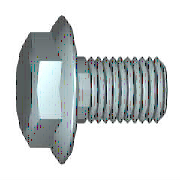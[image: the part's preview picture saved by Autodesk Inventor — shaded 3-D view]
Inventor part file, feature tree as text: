
AUTODESK INVENTOR PART (.ipt)
format: ipt  version: 2018 (Build 220112000, 112)  size: 210,944 bytes
history: native  units: mm (DEFAULTED — no unit token found)
features: sketch x3, other x2, extrude x1, plane x1
ambient origin geometry x7: Origin, YZ Plane, XZ Plane, X Axis, Y Axis, Z Axis, Center Point
bodies: Solid1 (feature_tree)
feature tree (7):
  other  "Corpo"
  extrude  "Testa"  Depth=1.1mm
  other  "Smusso1"
  plane  "Work Plane1"
  sketch  "Schizzo1"
  sketch  "Schizzo2"
  sketch  "Schizzo3"
